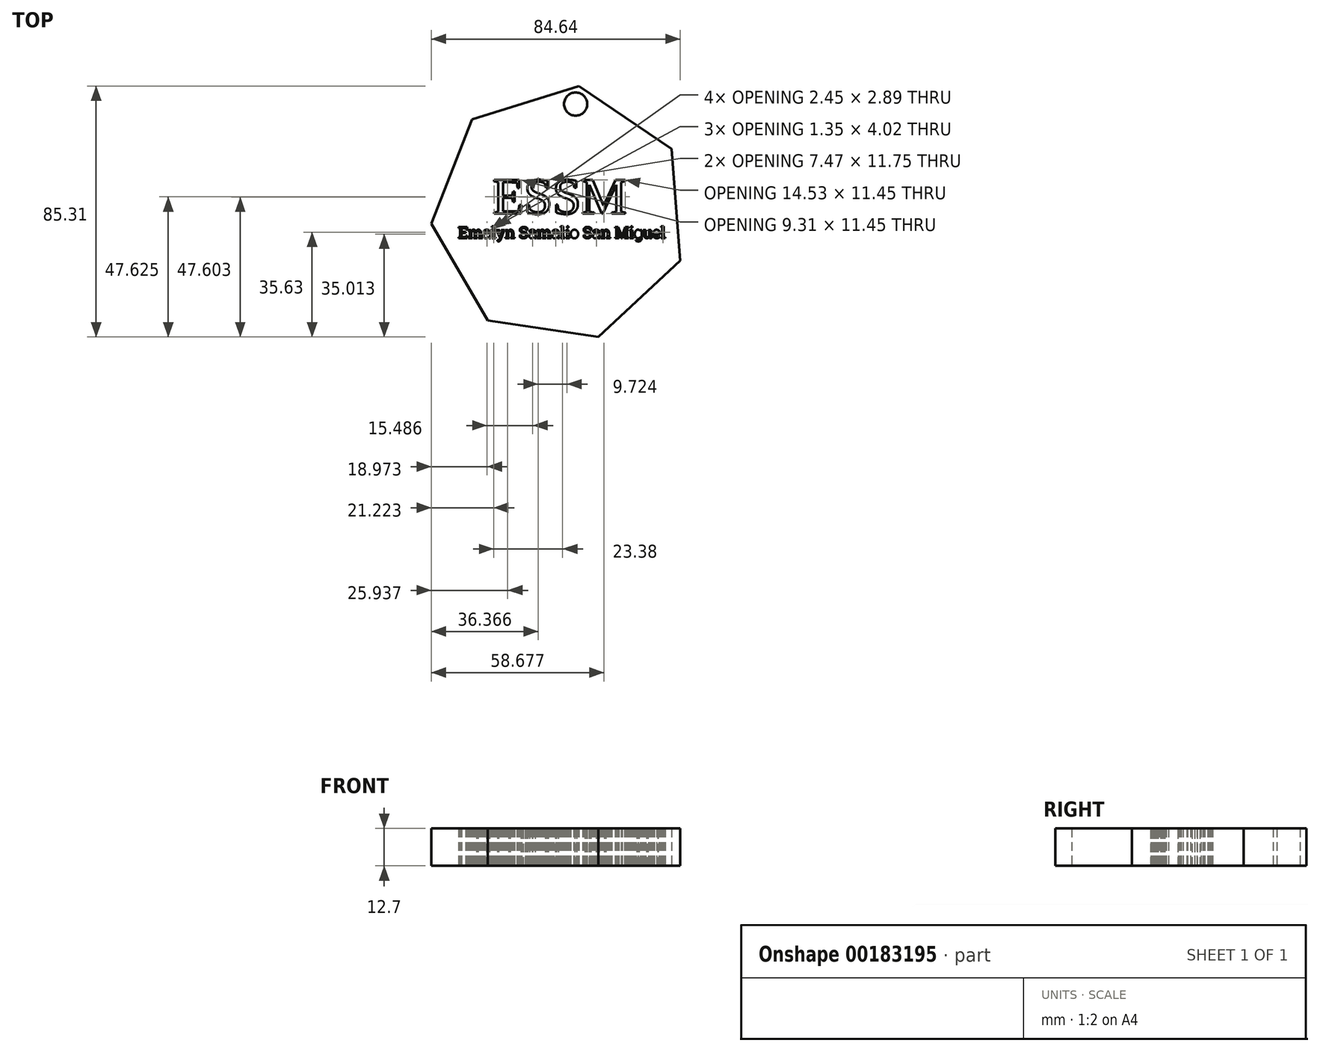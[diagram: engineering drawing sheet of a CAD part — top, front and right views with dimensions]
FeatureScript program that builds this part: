
annotation { "Feature Type Name" : "Feature", "Feature Type Description" : "" }
export const myFeature = defineFeature(function(context is Context, id is Id, definition is map)
    precondition{}
    {
        {
            var Q0;
            Q0=qCreatedBy(makeId("Top.planeOp"),FACE);
            var sketch = newSketch(context, id + "F0", { "sketchPlane" : qUnion([Q0])});
            skCircle(sketch, "E0.cCircle", {"center": v(0, 0) * mm, "radius": 39.54 * mm, "construction": true});
            skLineSegment(sketch, "E0.0", {"start": v(40.9, -15.92) * mm, "end": v(13.04, -41.9) * mm});
            skLineSegment(sketch, "E0.1", {"start": v(13.04, -41.9) * mm, "end": v(-24.62, -36.32) * mm});
            skLineSegment(sketch, "E0.2", {"start": v(-24.62, -36.32) * mm, "end": v(-43.75, -3.4) * mm});
            skLineSegment(sketch, "E0.3", {"start": v(-43.75, -3.4) * mm, "end": v(-29.93, 32.09) * mm});
            skLineSegment(sketch, "E0.4", {"start": v(-29.93, 32.09) * mm, "end": v(6.43, 43.4) * mm});
            skLineSegment(sketch, "E0.5", {"start": v(6.43, 43.4) * mm, "end": v(37.95, 22.04) * mm});
            skLineSegment(sketch, "E0.6", {"start": v(37.95, 22.04) * mm, "end": v(40.9, -15.92) * mm});
            skPoint(sketch, "E0.0.midPoint", {"position": v(26.97, -28.91) * mm});
            skText(sketch, "E1", { "text": "ESSM", "fontName": "Tinos-Regular.ttf"});
            skText(sketch, "E2", { "text": "Emalyn Samalio San Miguel ", "fontName": "RobotoSlab-Regular.ttf"});
            skCircle(sketch, "E3", {"center": v(5.3, 37.27) * mm, "radius": 3.94 * mm});
            const initialGuessF0  = {"E1": [-0.02297, 0, 1, 0, 0.01259], "E2": [-0.03462, -0.00828, 1, 0, 0.0038]};
            skSetInitialGuess(sketch, initialGuessF0);
            skSolve(sketch);
        }
        {
            var Q0;
            Q0=makeQuery(id+"F0.imprint","IMPRINT",FACE,{"disambiguationData":[TD([[makeQuery(id+"F0.imprint","IMPRINT",EDGE,{"derivedFrom":sQuery(id+"F0.wireOp",EDGE,"E0.0")}),-1.0]])]});
            extrude(context, id + "F1", {"entities" : qUnion([Q0]), "depth" : 12.7 * mm});
        }
    });
